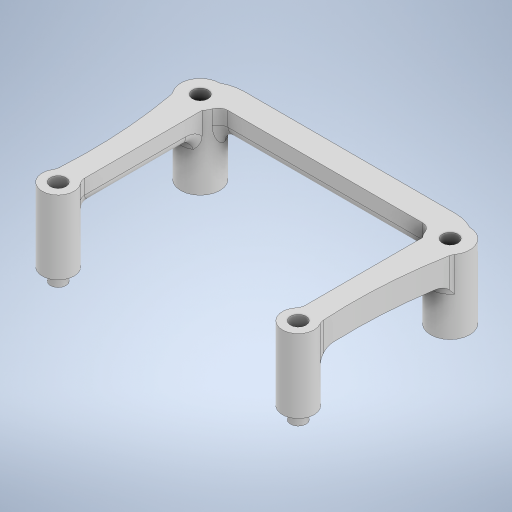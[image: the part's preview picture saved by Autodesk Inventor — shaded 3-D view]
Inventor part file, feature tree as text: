
AUTODESK INVENTOR PART (.ipt)
format: ipt  version: 2024.2 (Build 282272000, 272)  size: 475,136 bytes
history: native  units: mm
features: extrude x5, sketch x5, fillet x1, projected_geometry x1
ambient origin geometry x8: Origin, YZ Plane, XZ Plane, XY Plane, X Axis, Y Axis, Z Axis, Center Point
bodies: Solid1 (feature_tree)
feature tree (12):
  extrude  "Extrusion1"  Depth=5.0mm TaperAngle=0.0deg
  extrude  "Extrusion2"  Depth=5.2mm
  extrude  "Extrusion3"  Depth=8.0mm
  extrude  "Extrusion4"  Depth=49.0mm
  fillet  "Fillet1"  Radius=51.0mm
  extrude  "Extrusion5"  Depth=5.0mm
  sketch  "Sketch2"  dims[d0=6.5mm d1=5.0mm d2=0.0mm]
  sketch  "Sketch3"  dims[d3=6.5mm d4=5.2mm]
  sketch  "Sketch4"  dims[d5=5.2mm d6=8.0mm]
  projected_geometry  "Projected Loop1"
  sketch  "Sketch5"  dims[d7=8.0mm d8=49.0mm d9=51.0mm]
  sketch  "Sketch6"  dims[d11=30.0mm d12=3.2mm d13=3.2mm d14=2.5mm d15=0.0mm d16=3.0mm d17=3.0mm d18=5.0mm d19=0.0mm d21=1.0mm d24=100.0mm d25=100.0mm d26=2.5mm d27=3.0mm d28=3.0mm d29=2.5mm d30=5.0mm d31=0.0mm d32=5.0mm d33=4.0mm d34=4.0mm d35=2.0mm d36=5.0mm d37=0.0mm d38=3.2mm d39=3.2mm d40=3.0mm d41=3.0mm d20=0.5mm]
